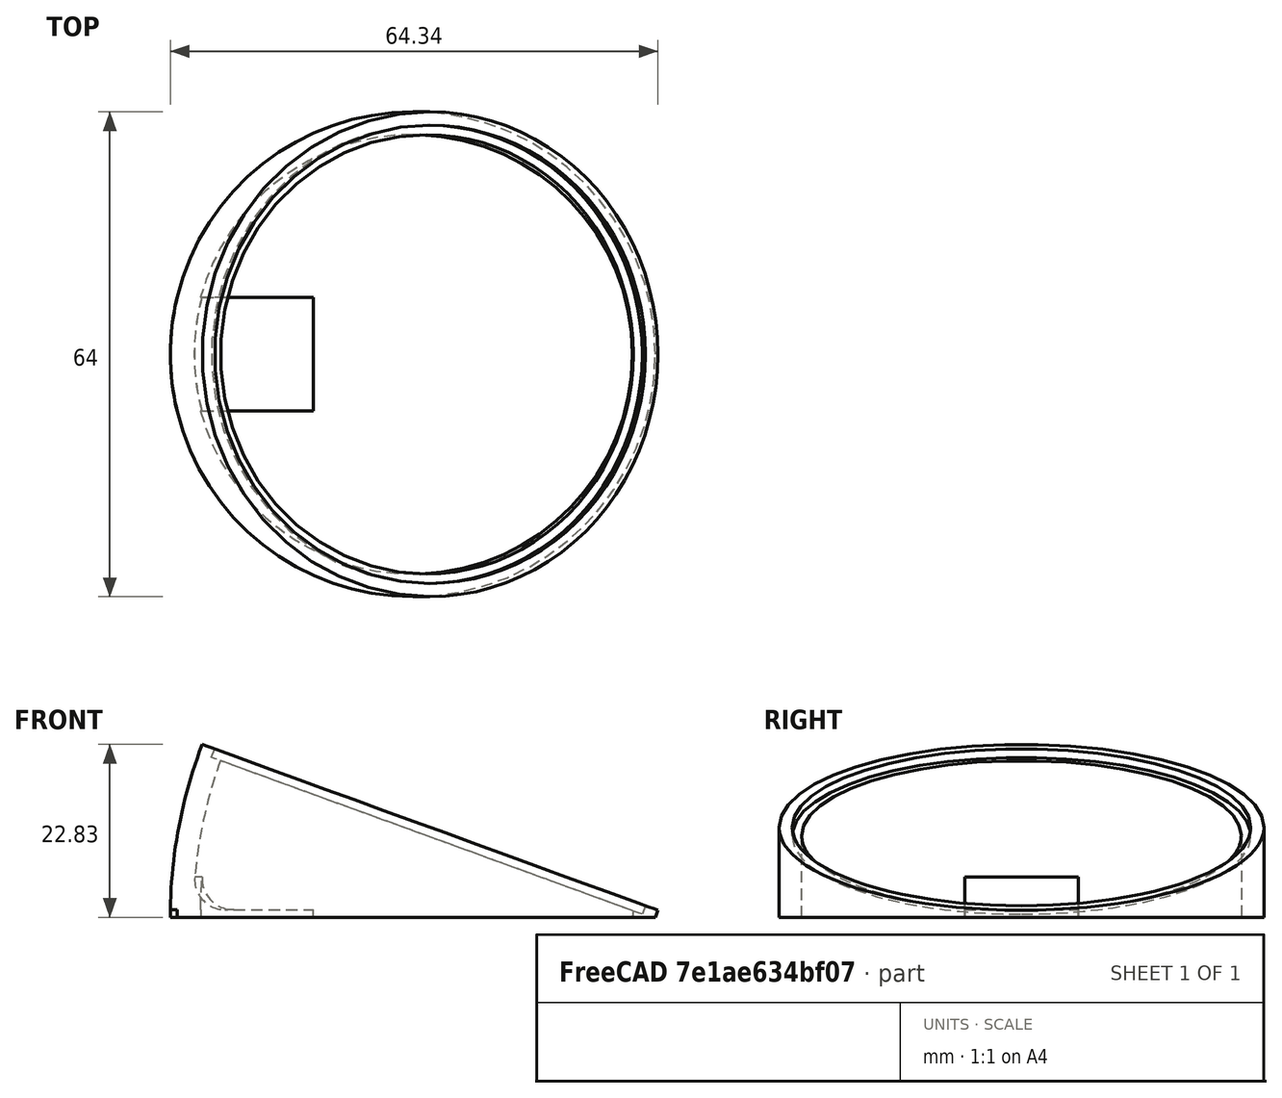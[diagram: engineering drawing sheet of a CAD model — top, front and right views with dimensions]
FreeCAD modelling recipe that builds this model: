
FCSTD DOCUMENT  (FreeCAD 0.20R)
Label: base
License: All rights reserved
LicenseURL: http://en.wikipedia.org/wiki/All_rights_reserved
objects: Sketcher::SketchObject×5, PartDesign::Pad×2, PartDesign::Revolution×1, PartDesign::Groove×1, PartDesign::Pocket×1, PartDesign::Fillet×1, PartDesign::Body×1
note: 18 computed .brp shape members not serialized (recipe doc carries the construction recipe); baked Part::Feature solids carry a one-line shape summary decoded from their .brp

FEATURE [Sketcher::SketchObject] Sketch
  FullyConstrained = true
  MapMode = 5
  Support = -> [XY_Plane]
  sketch-geometry (1):
    g0: Circle CenterX=-32 CenterY=0 CenterZ=0 NormalX=0 NormalY=0 NormalZ=1 AngleXU=0 Radius=32
  constraints (3):
    c: PointOnObject(g0,g-1)
    c: PointOnObject(g-1,g0)
    c: Diameter(g0) = 64
FEATURE [PartDesign::Revolution] Revolution
  Angle = 20
  Axis = (0,1,0)
  Base = (0,0,0)
  Profile = -> Sketch
  ReferenceAxis = -> Sketch [V_Axis]
FEATURE [Sketcher::SketchObject] Sketch001
  ExternalGeometry = -> [Revolution]
  FullyConstrained = true
  MapMode = 5
  Placement = pos=(0,0,0) rot=(1,0,0;3.14159rad)
  Support = -> [Revolution]
  sketch-geometry (1):
    g0: Circle CenterX=-32 CenterY=0 CenterZ=0 NormalX=0 NormalY=0 NormalZ=1 AngleXU=0 Radius=29
  constraints (2):
    c: Coincident(g0,g-3)
    c: Diameter(g0) = 58
FEATURE [PartDesign::Groove] Groove
  Angle = 360
  Axis = (0,-1,0)
  Base = (0,0,0)
  BaseFeature = -> Revolution
  Profile = -> Sketch001
  ReferenceAxis = -> Sketch001 [V_Axis]
  Reversed = true
FEATURE [Sketcher::SketchObject] Sketch002
  ExternalGeometry = -> [Groove]
  FullyConstrained = true
  MapMode = 5
  Placement = pos=(0,0,0) rot=(0,1,0;0.349066rad)
  Support = -> [Groove]
  sketch-geometry (1):
    g0: Circle CenterX=-32 CenterY=0 CenterZ=0 NormalX=0 NormalY=0 NormalZ=1 AngleXU=0 Radius=32
  constraints (2):
    c: Coincident(g0,g-3)
    c: PointOnObject(g-1,g0)
FEATURE [PartDesign::Pad] Pad
  BaseFeature = -> Groove
  Direction = (0.34202,0,0.939693)
  Length = 1
  Length2 = 10
  Profile = -> Sketch002
  ReferenceAxis = -> Sketch002 [N_Axis]
  Type = 0
FEATURE [Sketcher::SketchObject] Sketch003
  ExternalGeometry = -> [Pad]
  FullyConstrained = true
  MapMode = 5
  Placement = pos=(0.34202,0,0.939693) rot=(0,1,0;0.349066rad)
  Support = -> [Pad]
  sketch-geometry (1):
    g0: Circle CenterX=-32 CenterY=0 CenterZ=0 NormalX=0 NormalY=0 NormalZ=1 AngleXU=0 Radius=30.25
  constraints (2):
    c: Coincident(g0,g-3)
    c: Diameter(g0) = 60.5
FEATURE [PartDesign::Pocket] Pocket
  BaseFeature = -> Pad
  Direction = (-0.34202,0,-0.939693)
  Length = 1.2
  Length2 = 5
  Profile = -> Sketch003
  ReferenceAxis = -> Sketch003 [N_Axis]
  Type = 0
FEATURE [Sketcher::SketchObject] Sketch004
  ExternalGeometry = -> [Pocket]
  FullyConstrained = false
  MapMode = 5
  Placement = pos=(0,0,0) rot=(1,0,0;3.14159rad)
  Support = -> [Pocket]
  sketch-geometry (4):
    g0: LineSegment StartX=-63.1087 StartY=7.5 StartZ=0 EndX=-45.1087 EndY=7.5 EndZ=0
    g1: LineSegment StartX=-45.1087 StartY=7.5 StartZ=0 EndX=-45.1087 EndY=-7.5 EndZ=0
    g2: LineSegment StartX=-45.1087 StartY=-7.5 StartZ=0 EndX=-63.1087 EndY=-7.5 EndZ=0
    g3: ArcOfCircle CenterX=-32 CenterY=0 CenterZ=0 NormalX=0 NormalY=0 NormalZ=1 AngleXU=0 Radius=32 StartAngle=2.90502 EndAngle=3.37817
  constraints (10):
    c: Coincident(g0,g1)
    c: Coincident(g1,g2)
    c: Horizontal(g0)
    c: Horizontal(g2)
    c: Coincident(g3,g2)
    c: Coincident(g3,g0)
    c: Symmetric(g1,g0,g-1)
    c: Distance(g1) = 15
    c: Distance(g0) = 18
    c: Coincident(g-3,g3)
FEATURE [PartDesign::Pad] Pad001
  BaseFeature = -> Pocket
  Direction = (0,0,-1)
  Length = 1
  Length2 = 10
  Profile = -> Sketch004
  ReferenceAxis = -> Sketch004 [N_Axis]
  Reversed = true
  Type = 0
FEATURE [PartDesign::Fillet] Fillet
  Base = -> Pad001 [Edge22]
  BaseFeature = -> Pad001
  Radius = 4
  SupportTransform = false
  UseAllEdges = false
FEATURE [PartDesign::Body] Body
  Group = -> [Sketch,Revolution,Sketch001,Groove,Sketch002,Pad,Sketch003,Pocket,Sketch004,Pad001,Fillet]
  Origin = -> Origin
  Tip = -> Fillet
